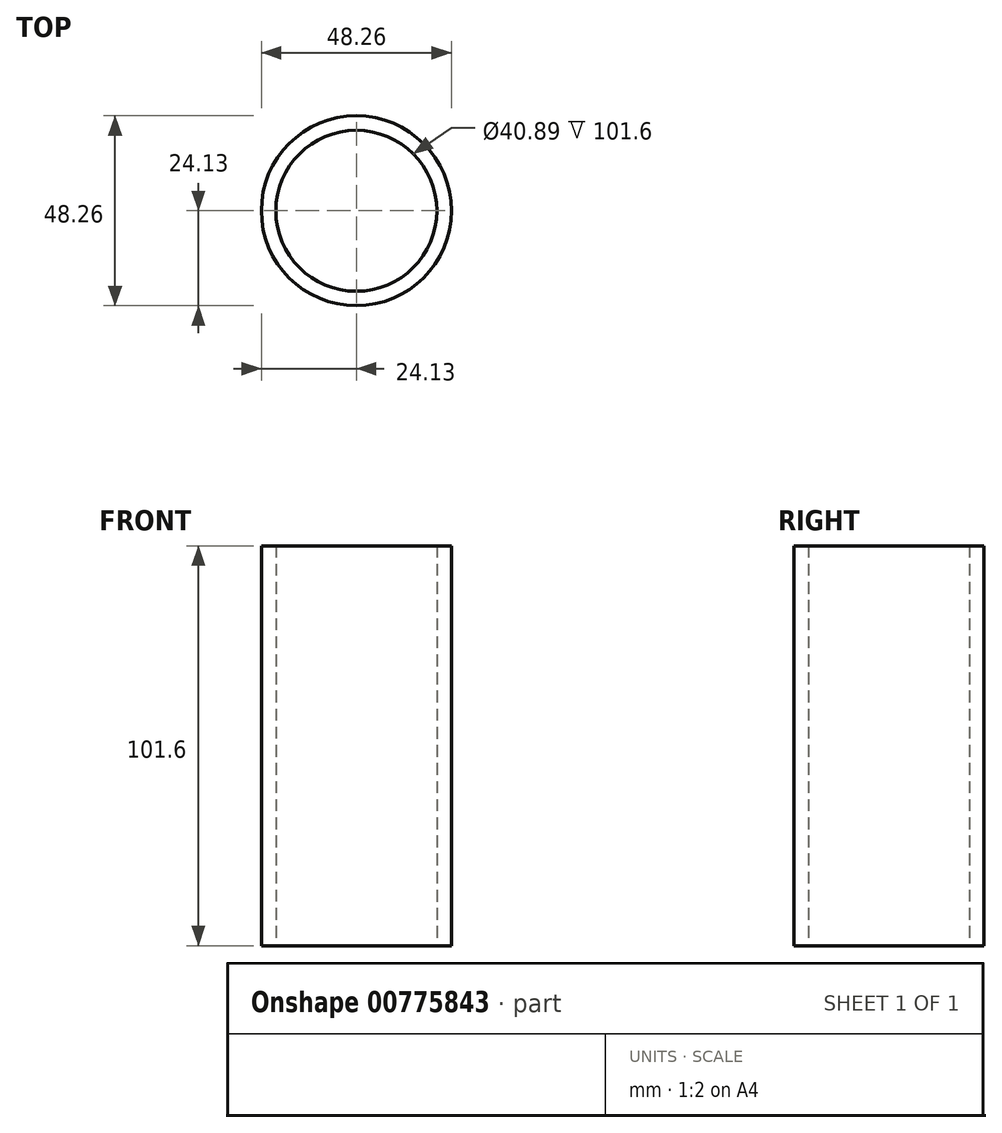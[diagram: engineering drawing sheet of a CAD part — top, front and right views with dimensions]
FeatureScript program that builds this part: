
annotation { "Feature Type Name" : "Feature", "Feature Type Description" : "" }
export const myFeature = defineFeature(function(context is Context, id is Id, definition is map)
    precondition{}
    {
        {
            var Q0;
            Q0=qCreatedBy(makeId("Top.planeOp"),FACE);
            var sketch = newSketch(context, id + "F0", { "sketchPlane" : qUnion([Q0])});
            skCircle(sketch, "E0", {"center": v(0, 0) * mm, "radius": 24.13 * mm});
            skCircle(sketch, "E1", {"center": v(0, 0) * mm, "radius": 20.45 * mm});
            skSolve(sketch);
        }
        {
            var Q0;
            Q0=makeQuery(id+"F0.imprint","IMPRINT",FACE,{"disambiguationData":[TD([[makeQuery(id+"F0.imprint","IMPRINT",EDGE,{"derivedFrom":sQuery(id+"F0.wireOp",EDGE,"E0")}),1.0]])]});
            extrude(context, id + "F1", {"entities" : qUnion([Q0]), "depth" : 101.6 * mm, "offsetDistance" : 25.4 * mm});
        }
    });
